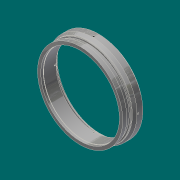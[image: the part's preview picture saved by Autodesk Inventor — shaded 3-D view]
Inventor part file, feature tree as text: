
AUTODESK INVENTOR PART (.ipt)
format: ipt  version: 2017.3 (Build 213256000, 256)  size: 237,056 bytes
history: native  units: in
note: dims shown in document units (in); Inventor stores cm internally (conversion verified against a paired STEP export)
features: sketch x2, hole x2, revolve x1, chamfer x1, fillet x1, plane x1, pattern_circular x1
ambient origin geometry x8: Origin, YZ Plane, XZ Plane, XY Plane, X Axis, Y Axis, Z Axis, Center Point
bodies: Solid1 (feature_tree)
feature tree (9):
  revolve  "Revolution1"  Angle=90.0deg
  chamfer  "Chamfer2"  Distance=17.25in
  fillet  "Fillet1"  Radius=1.75in
  plane  "Work Plane1"
  sketch  "Sketch5"  dims[d13=16.75in d14=17.25in d16=1.75in d17=1.35in d18=0.0515in d19=0.0842in d20=0.0312in d21=0.125in d22=45.0deg d32=18.0in d33=0.5625in d34=0.125in d35=0.0625in d36=0.5in d37=30.0deg d38=8.0in d39=0.25in d40=0.5in d41=60.0deg d42=0.5in d44=0.688in d45=0.534in d46=0.0246in d47=0.688in d48=0.375in d49=0.25in d50=0.5635in d51=0.891in d52=0.8108in d53=0.417in d54=1.5in d55=0.375in d56=0.25in d57=0.5635in d58=3.0in d59=0.8108in d67=1.5748in d68=360.0deg d72=6.0in d73=0.0312in d75=1.0in d78=30.0deg d80=0.0376in d81=0.5in d82=0.25in d83=5.5in d84=15.9375in]
  hole  "Hole1"  [1 undecoded]
  hole  "Hole2"  [1 undecoded]
  pattern_circular  "Circular Pattern2"  [2 undecoded]
  sketch  "Sketch1"  dims[d0=15.8in d6=90.0deg]
note: 4 required parameter values undecoded (feature->parameter linkage not recoverable at this tier; creation-order binding heuristic only, values carry confidence <= 0.55)
